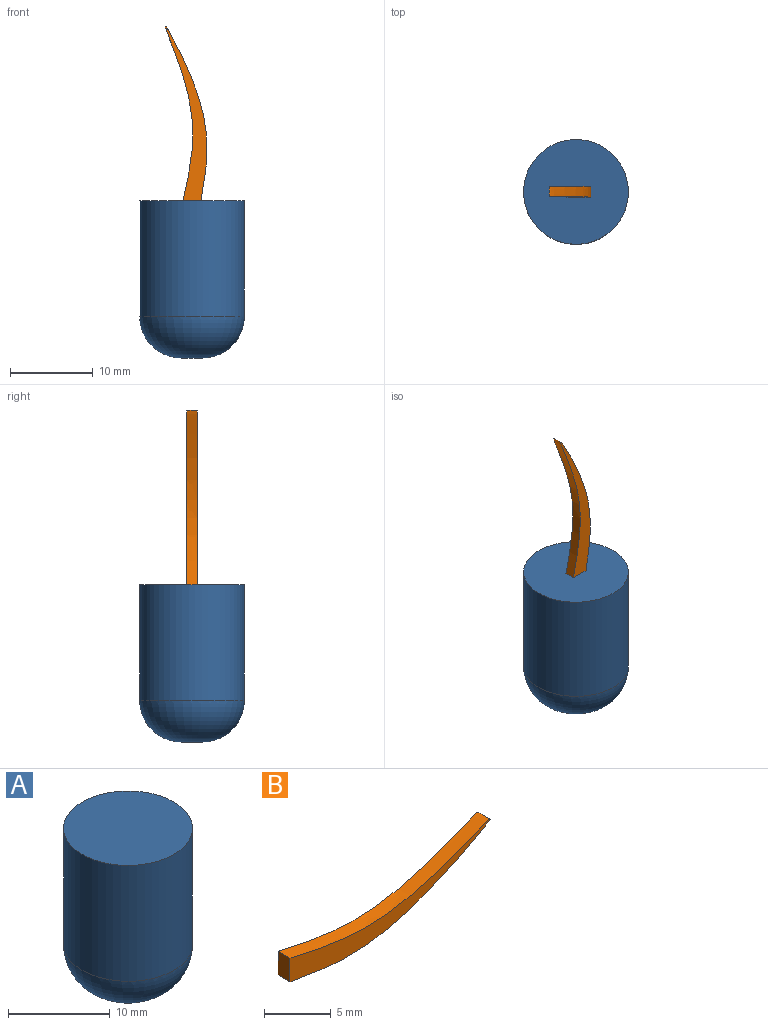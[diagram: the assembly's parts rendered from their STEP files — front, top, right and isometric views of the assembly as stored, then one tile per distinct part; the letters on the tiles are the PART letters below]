
ASSEMBLY  parts=2 mates=1
PART A: 4 faces, bbox 12.7x12.7x19.1 mm
  f0: cylinder r=6.35mm len=13.97mm, axis (0,0,-1), area 557.4mm2, adj f1,f3
  f1: plane 12.7x12.7mm, normal (0,0,1), area 126.7mm2, adj f0
  f2: plane 2.54x2.54mm, normal (0,0,-1), area 5.1mm2, adj f3
  f3: torus R=1.27mm, axis (0,0,1), area 225.8mm2, adj f0,f2
PART B: 4 faces, bbox 21.8x1.3x6.2 mm
  f0: extruded ~21.17x5.06mm, area 56.4mm2, adj f1,f2,f3
  f1: plane 2.17x1.27mm, normal (-1,0,0), area 2.8mm2, adj f0,f2,f3
  f2: plane 21.76x6.22mm, normal (0,-1,0), area 28.4mm2, adj f0,f1
  f3: plane 21.76x6.22mm, normal (0,1,0), area 28.4mm2, adj f0,f1
PLACE A t=(-16.15,7.29,9.44)mm
PLACE B rot(axis=(0,-1,0),90deg) t=(-17.24,7.92,28.49)mm
MATE fastened A.f0 <-> B.f1  axis (0,0,1) through (-16.15,7.29,28.49)mm
